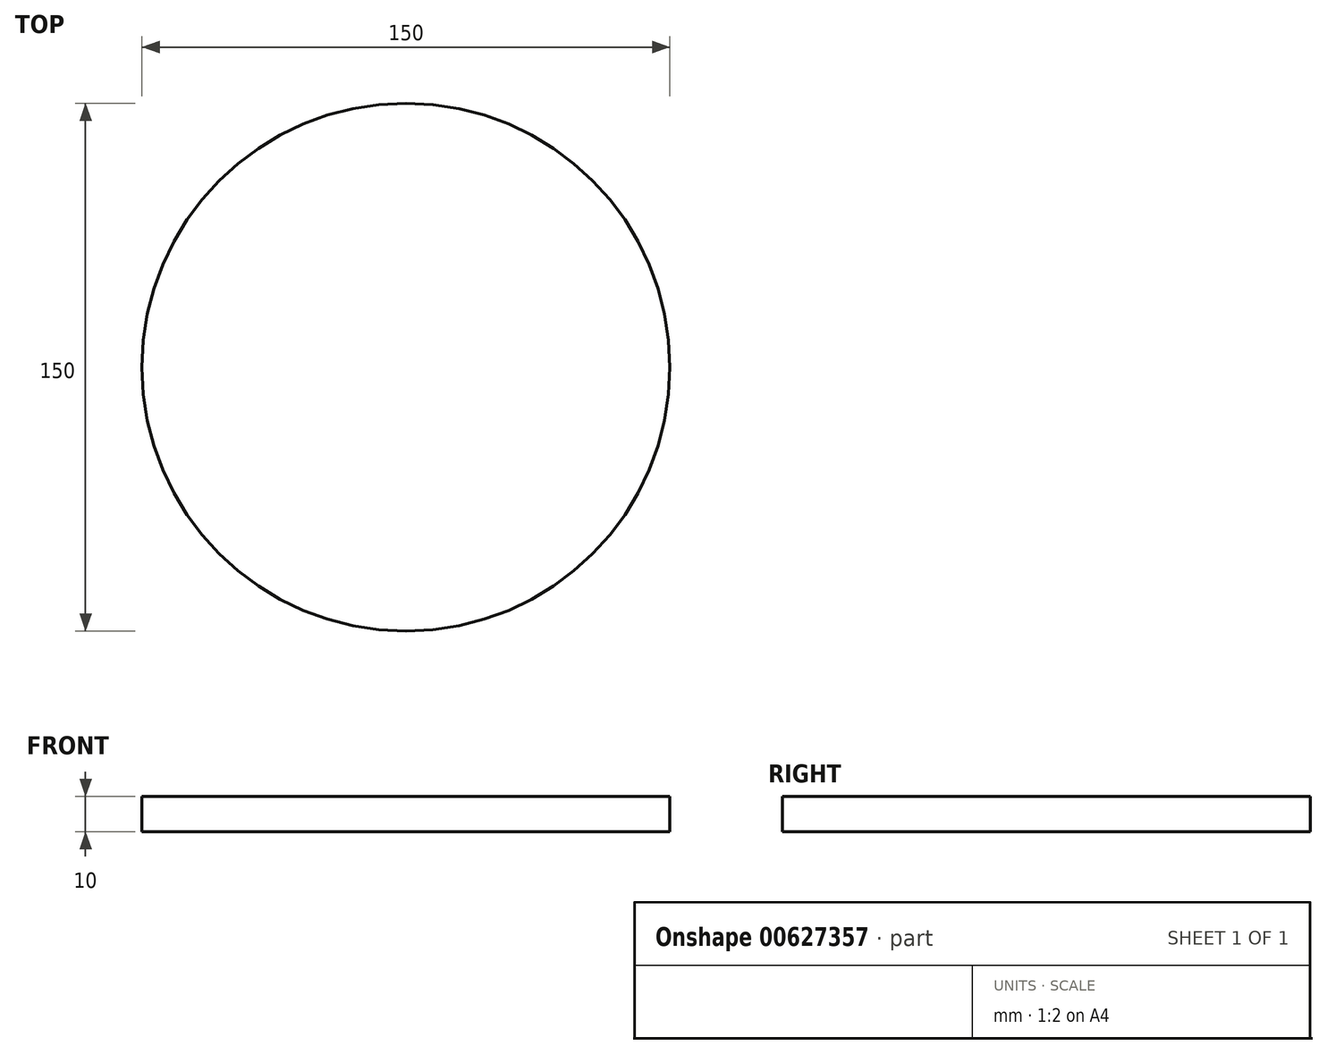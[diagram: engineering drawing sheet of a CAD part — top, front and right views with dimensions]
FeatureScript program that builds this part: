
annotation { "Feature Type Name" : "Feature", "Feature Type Description" : "" }
export const myFeature = defineFeature(function(context is Context, id is Id, definition is map)
    precondition{}
    {
        {
            var Q0;
            Q0=qCreatedBy(makeId("Top.planeOp"),FACE);
            var sketch = newSketch(context, id + "F0", { "sketchPlane" : qUnion([Q0])});
            skCircle(sketch, "E0", {"center": v(0, 0) * mm, "radius": 75 * mm});
            skSolve(sketch);
        }
        {
            var Q0;
            Q0=makeQuery(id+"F0.imprint","IMPRINT",FACE,{"disambiguationData":[TD([[makeQuery(id+"F0.imprint","IMPRINT",EDGE,{"derivedFrom":sQuery(id+"F0.wireOp",EDGE,"E0")}),1.0]])]});
            extrude(context, id + "F1", {"entities" : qUnion([Q0]), "depth" : 10 * mm, "offsetDistance" : 25 * mm});
        }
    });
